# Revit family: Mezcladora para Lavabo MP-1000
name_source: partatom
category: Aparatos sanitarios
revit_build: Autodesk Revit 2016 (Build: 20150220_1215(x64)
units: mm (PartAtom-declared; Revit-internal decimal feet)

## family parameters
Compartido = Sí
Corte con vacíos al cargar = No
Cota de conector redondo = Diámetro de uso
Número OmniClass = 23.45.55.17
Punto de cálculo de habitación = Sí
Se basa en plano de trabajo = Sí
Siempre vertical = Sí
Tipo de pieza = Normal
Título OmniClass = Mixing Faucets

## types (1)
- MP-1000
    Brass Chromed = Brass
    Comentarios de tipo = Lavatory Faucet Assemblies
    Data Sheet = http://www.helvex.com.mx
    Descripción = 12" Vertika Assembly With Push Drain
    Elevación por defecto = 1"
    Fabricante = HELVEX
    Features = For Use With Magna II Handle; Val-vex V Ceramic Discs To ¼ Turn; Installtion 8", 10" Or 12"; Push Drain With Overflow; Includes Handles; Includes Tool For Securing; Includes Wrench Maintenance
    Imagen de tipo = MP-1000.JPG
    Inlet Threads = ½" - 14 NPSM
    Instructive = http://www.helvex.com.mx
    Max. Water Flow = 1.3 gal/min
    Max. Working Pressure = 85.3 psi
    Min. Working Pressure = 14.2 psi
    Modelo = MP-1000
    Note = 41A Is Used For Valvex  Which You Can Change The Direction Of Rotation, Left Or Right
    Satin = Satín
    Support Base Diameter = 2"
    Total Height = 4"
    Total Length = 12"
    Total Width = 8"
    URL = http://www.helvex.com.mx

## geometry (parser evidence)
native form markers: Sweep x3
no freeform markers — native parametric forms only
